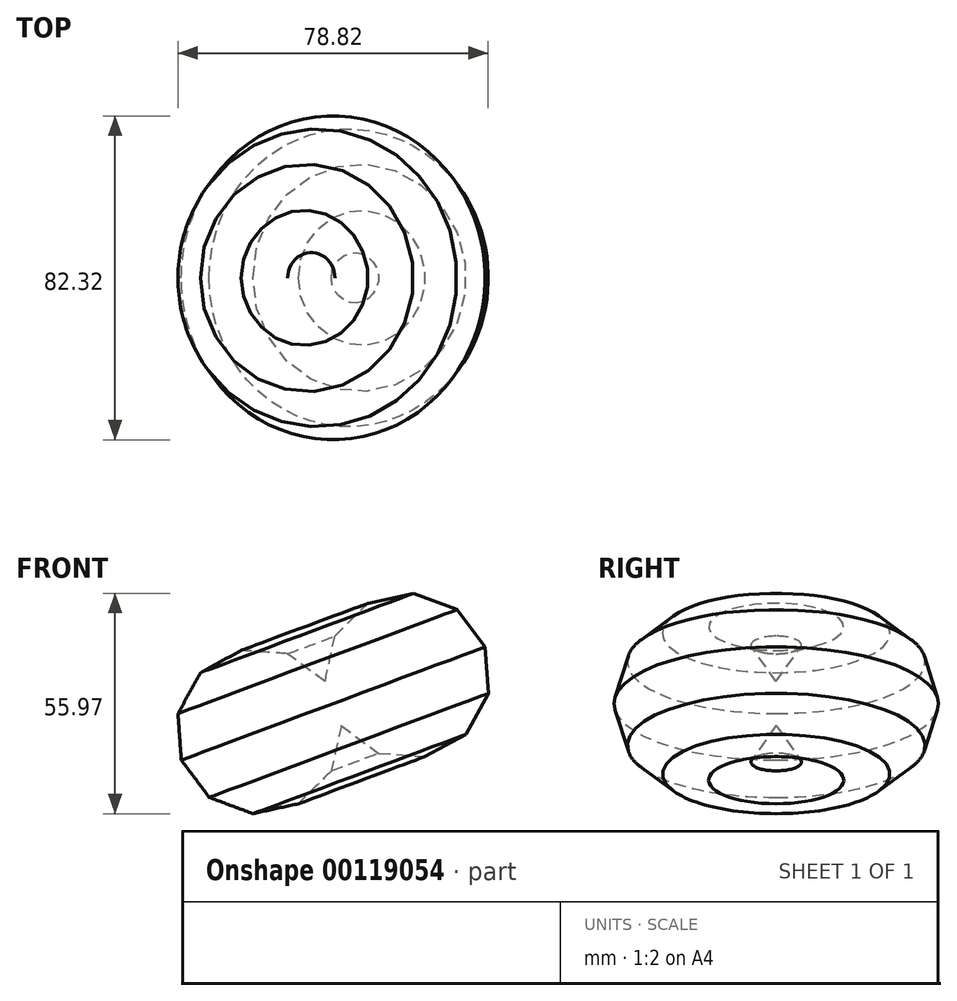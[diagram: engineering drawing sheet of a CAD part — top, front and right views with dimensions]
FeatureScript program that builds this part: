
annotation { "Feature Type Name" : "Feature", "Feature Type Description" : "" }
export const myFeature = defineFeature(function(context is Context, id is Id, definition is map)
    precondition{}
    {
        {
            var Q0;
            Q0=qCreatedBy(makeId("Front.planeOp"),FACE);
            var sketch = newSketch(context, id + "F0", { "sketchPlane" : qUnion([Q0])});
            skCircle(sketch, "E0.cCircle", {"center": v(0, 0) * mm, "radius": 20.15 * mm, "construction": true});
            skLineSegment(sketch, "E0.0", {"start": v(-7.35, -19.68) * mm, "end": v(-16.82, -12.58) * mm});
            skLineSegment(sketch, "E0.1", {"start": v(-16.82, -12.58) * mm, "end": v(-20.95, -1.49) * mm});
            skLineSegment(sketch, "E0.2", {"start": v(-20.95, -1.49) * mm, "end": v(-18.43, 10.08) * mm});
            skLineSegment(sketch, "E0.3", {"start": v(-18.43, 10.08) * mm, "end": v(-10.06, 18.44) * mm});
            skLineSegment(sketch, "E0.4", {"start": v(-10.06, 18.44) * mm, "end": v(1.5, 20.95) * mm});
            skLineSegment(sketch, "E0.5", {"start": v(1.5, 20.95) * mm, "end": v(12.6, 16.8) * mm});
            skLineSegment(sketch, "E0.6", {"start": v(12.6, 16.8) * mm, "end": v(19.68, 7.33) * mm});
            skLineSegment(sketch, "E0.7", {"start": v(19.68, 7.33) * mm, "end": v(20.52, -4.47) * mm});
            skLineSegment(sketch, "E0.8", {"start": v(20.52, -4.47) * mm, "end": v(14.85, -14.86) * mm});
            skLineSegment(sketch, "E0.9", {"start": v(14.85, -14.86) * mm, "end": v(4.46, -20.53) * mm});
            skLineSegment(sketch, "E0.10", {"start": v(4.46, -20.53) * mm, "end": v(-7.35, -19.68) * mm});
            skPoint(sketch, "E0.0.midPoint", {"position": v(-12.09, -16.13) * mm});
            skSolve(sketch);
        }
        {
            var Q0;
            Q0=makeQuery(id+"F0.imprint","IMPRINT",FACE,{"disambiguationData":[TD([[makeQuery(id+"F0.imprint","IMPRINT",EDGE,{"derivedFrom":sQuery(id+"F0.wireOp",EDGE,"E0.0")}),-1.0]])]});
            var Q1;
            Q1=sQuery(id+"F0.wireOp",EDGE,"E0.1");
            revolve(context, id + "F1", {"entities" : qUnion([Q0]), "axis" : qUnion([Q1]), "revolveType" : RevolveType.FULL});
        }
    });
